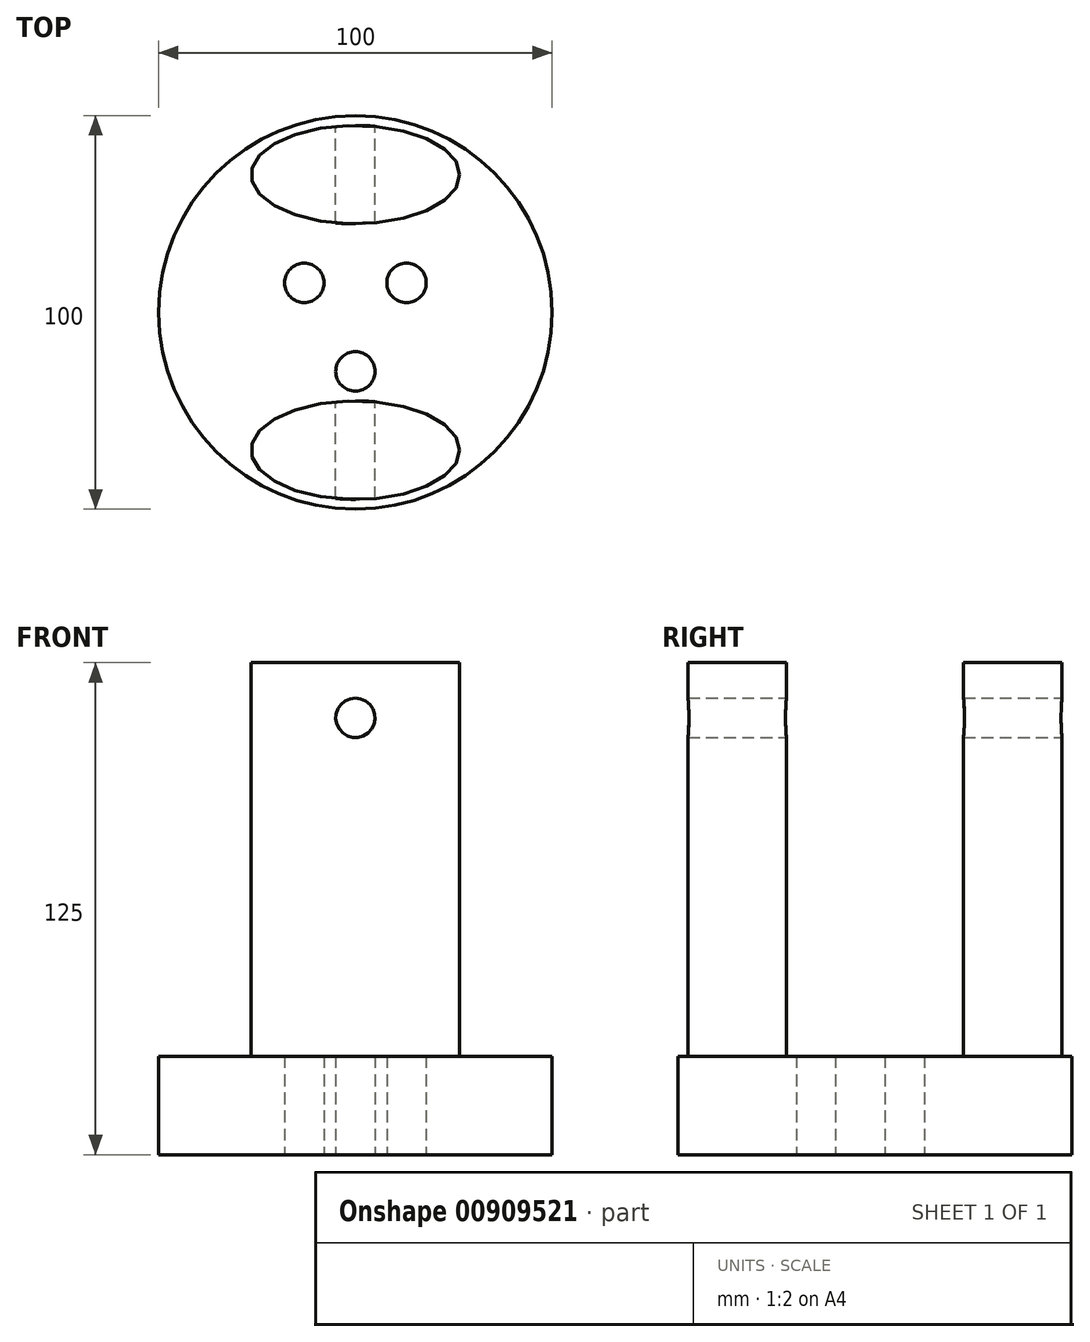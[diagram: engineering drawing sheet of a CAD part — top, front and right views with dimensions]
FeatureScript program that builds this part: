
annotation { "Feature Type Name" : "Feature", "Feature Type Description" : "" }
export const myFeature = defineFeature(function(context is Context, id is Id, definition is map)
    precondition{}
    {
        {
            var Q0;
            Q0=qCreatedBy(makeId("Top.planeOp"),FACE);
            var sketch = newSketch(context, id + "F0", { "sketchPlane" : qUnion([Q0])});
            skCircle(sketch, "E0", {"center": v(0, 0) * mm, "radius": 50 * mm});
            skCircle(sketch, "E1", {"center": v(0, -15) * mm, "radius": 5 * mm});
            skCircle(sketch, "E2.1.0", {"center": v(13, 7.5) * mm, "radius": 5 * mm});
            skCircle(sketch, "E2.2.0", {"center": v(-13, 7.5) * mm, "radius": 5 * mm});
            skSolve(sketch);
        }
        {
            var Q0;
            Q0=makeQuery(id+"F0.imprint","IMPRINT",FACE,{"disambiguationData":[TD([[makeQuery(id+"F0.imprint","IMPRINT",EDGE,{"derivedFrom":sQuery(id+"F0.wireOp",EDGE,"E0")}),1.0]])]});
            extrude(context, id + "F1", {"entities" : qUnion([Q0]), "depth" : 25 * mm, "offsetDistance" : 25 * mm});
        }
        {
            var Q0;
            Q0=makeQuery(id+"F1.opExtrude","CAP_FACE",FACE,{"disambiguationData":[OSD([sQuery(id+"F0.wireOp",EDGE,"E0"),sQuery(id+"F0.wireOp",EDGE,"E1"),sQuery(id+"F0.wireOp",EDGE,"E2.1.0"),sQuery(id+"F0.wireOp",EDGE,"E2.2.0")])],"isStart":false});
            var sketch = newSketch(context, id + "F2", { "sketchPlane" : qUnion([Q0])});
            skEllipse(sketch, "E3", {"center": v(0, 35) * mm, "majorRadius": 26.5 * mm, "minorRadius": 12.5 * mm, "majorAxis": v(1, 0)});
            skLineSegment(sketch, "E4", {"start": v(-26.5, 73.55) * mm, "end": v(-26.5, -63.83) * mm, "construction": true});
            skPoint(sketch, "E4.startSnap0", {"position": v(-26.5, 35) * mm});
            skPoint(sketch, "E4.endSnap0", {"position": v(-26.5, 35) * mm});
            skEllipse(sketch, "E5", {"center": v(0, -35) * mm, "majorRadius": 26.5 * mm, "minorRadius": 12.5 * mm, "majorAxis": v(1, 0)});
            skPoint(sketch, "E6.startSnap0", {"position": v(26.5, 35) * mm});
            skPoint(sketch, "E7.startSnap0", {"position": v(26.5, -35) * mm});
            skPoint(sketch, "E7.endSnap0", {"position": v(26.5, -35) * mm});
            skLineSegment(sketch, "E8", {"start": v(0, 22.5) * mm, "end": v(-75.52, 22.5) * mm, "construction": true});
            skLineSegment(sketch, "E9", {"start": v(0, -22.5) * mm, "end": v(-78.35, -22.5) * mm, "construction": true});
            skSolve(sketch);
        }
        {
            var Q0;
            Q0=makeQuery(id+"F2.imprint","IMPRINT",FACE,{"disambiguationData":[TD([[makeQuery(id+"F2.imprint","IMPRINT",EDGE,{"derivedFrom":sQuery(id+"F2.wireOp",EDGE,"E3")}),1.0]])]});
            var Q1;
            Q1=makeQuery(id+"F2.imprint","IMPRINT",FACE,{"disambiguationData":[TD([[makeQuery(id+"F2.imprint","IMPRINT",EDGE,{"derivedFrom":sQuery(id+"F2.wireOp",EDGE,"E5")}),1.0]])]});
            extrude(context, id + "F3", {"entities" : qUnion([Q0, Q1]), "operationType" : NewBodyOperationType.ADD, "depth" : 100 * mm, "offsetDistance" : 25 * mm});
        }
        {
            var Q0;
            Q0=qCreatedBy(makeId("Front.planeOp"),FACE);
            var sketch = newSketch(context, id + "F4", { "sketchPlane" : qUnion([Q0])});
            skCircle(sketch, "E10", {"center": v(0, 111) * mm, "radius": 5 * mm});
            skSolve(sketch);
        }
        {
            var Q0;
            Q0=makeQuery(id+"F4.imprint","IMPRINT",FACE,{"disambiguationData":[TD([[makeQuery(id+"F4.imprint","IMPRINT",EDGE,{"derivedFrom":sQuery(id+"F4.wireOp",EDGE,"E10")}),1.0]])]});
            var Q1;
            Q1=makeQuery(id+"F3.opExtrude","SWEPT_FACE",FACE,{"disambiguationData":[OSD([sQuery(id+"F2.wireOp",EDGE,"E5")])]});
            var Q2;
            Q2=makeQuery(id+"F1.opExtrude","SWEPT_BODY",BODY,{"disambiguationData":[OSD([sQuery(id+"F0.wireOp",EDGE,"E0"),sQuery(id+"F0.wireOp",EDGE,"E1"),sQuery(id+"F0.wireOp",EDGE,"E2.1.0"),sQuery(id+"F0.wireOp",EDGE,"E2.2.0")])]});
            extrude(context, id + "F5", {"entities" : qUnion([Q0]), "operationType" : NewBodyOperationType.REMOVE, "endBound" : BoundingType.THROUGH_ALL, "depth" : 95 * mm, "endBoundEntityFace" : qUnion([Q1]), "endBoundEntityBody" : qUnion([Q2]), "offsetDistance" : 25 * mm, "hasSecondDirection" : true, "secondDirectionBound" : SecondDirectionBoundingType.THROUGH_ALL, "secondDirectionOppositeDirection" : true, "secondDirectionDepth" : 25 * mm});
        }
    });
